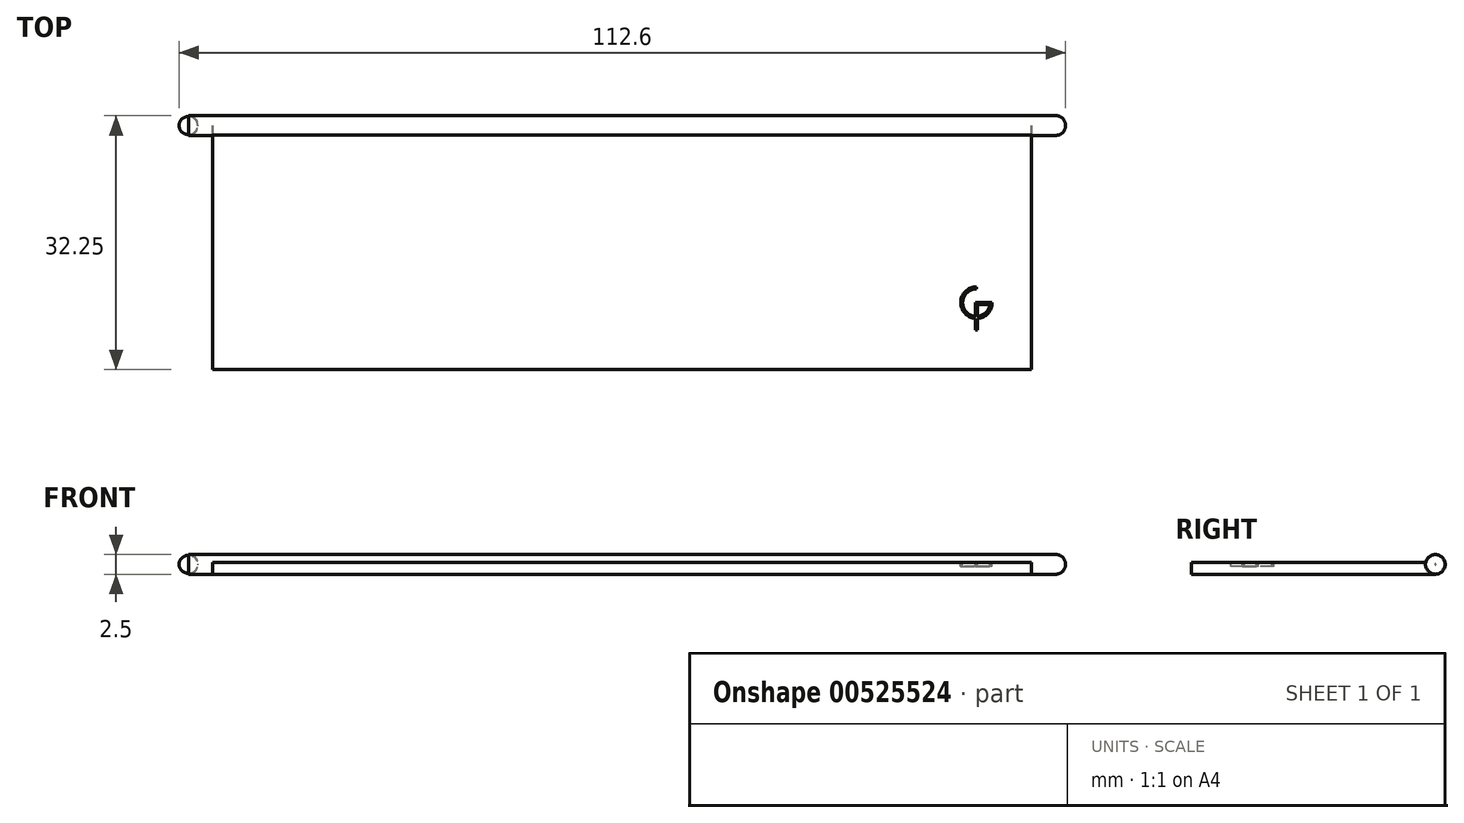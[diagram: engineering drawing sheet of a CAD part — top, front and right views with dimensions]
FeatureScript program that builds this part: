
annotation { "Feature Type Name" : "Feature", "Feature Type Description" : "" }
export const myFeature = defineFeature(function(context is Context, id is Id, definition is map)
    precondition{}
    {
        {
            var Q0;
            Q0=qCreatedBy(makeId("Right.planeOp"),FACE);
            var sketch = newSketch(context, id + "F0", { "sketchPlane" : qUnion([Q0])});
            skLineSegment(sketch, "E0.bottom", {"start": v(0, 0) * mm, "end": v(-31, 0) * mm});
            skLineSegment(sketch, "E0.top", {"start": v(0, 1.5) * mm, "end": v(-31, 1.5) * mm});
            skLineSegment(sketch, "E0.right", {"start": v(-31, 0) * mm, "end": v(-31, 1.5) * mm});
            skCircle(sketch, "E1", {"center": v(0, 1.25) * mm, "radius": 1.25 * mm});
            skPoint(sketch, "E1.second.point", {"position": v(0.68, 0.2) * mm});
            skPoint(sketch, "E1.third.point", {"position": v(-0.22, 2.48) * mm});
            skLineSegment(sketch, "E2", {"start": v(0, 1.5) * mm, "end": v(0, 0) * mm});
            skSolve(sketch);
        }
        {
            var Q0;
            {var subQ0=sQuery(id+"F0.wireOp",EDGE,"E0.bottom");Q0=makeQuery(id+"F0.imprint","IMPRINT",FACE,{"disambiguationData":[TD([[makeQuery(id+"F0.imprint","IMPRINT",EDGE,{"derivedFrom":subQ0}),-1.0]])]});}
            extrude(context, id + "F1", {"entities" : qUnion([Q0]), "oppositeDirection" : true, "depth" : 104 * mm, "offsetDistance" : 25 * mm});
        }
        {
            var Q0;
            {var subQ0=sQuery(id+"F0.wireOp",EDGE,"E2");Q0=makeQuery(id+"F0.imprint","IMPRINT",FACE,{"disambiguationData":[TD([[makeQuery(id+"F0.imprint","IMPRINT",EDGE,{"derivedFrom":subQ0}),-1.0]])]});}
            var Q1;
            {var subQ0=sQuery(id+"F0.wireOp",EDGE,"E2");Q1=makeQuery(id+"F0.imprint","IMPRINT",FACE,{"disambiguationData":[TD([[makeQuery(id+"F0.imprint","IMPRINT",EDGE,{"derivedFrom":subQ0}),1.0]])]});}
            extrude(context, id + "F2", {"entities" : qUnion([Q0, Q1]), "operationType" : NewBodyOperationType.ADD, "depth" : 4.3 * mm, "offsetDistance" : 25 * mm, "hasSecondDirection" : true, "secondDirectionOppositeDirection" : true, "secondDirectionDepth" : 108.3 * mm});
        }
        {
            var Q0;
            Q0=makeQuery(id+"F2.opExtrude","CAP_FACE",FACE,{"disambiguationData":[OSD([sQuery(id+"F0.wireOp",EDGE,"E1")])],"isStart":false});
            var Q1;
            Q1=makeQuery(id+"F2.opExtrude","CAP_FACE",FACE,{"disambiguationData":[OSD([sQuery(id+"F0.wireOp",EDGE,"E1")])],"isStart":true});
            fillet(context, id + "F3", {"entities" : qUnion([Q0, Q1]), "radius" : 1.2 * mm, "tangentPropagation" : true, "allowEdgeOverflow" : false});
        }
        {
            var Q0;
            Q0=makeQuery(id+"F1.opExtrude","SWEPT_FACE",FACE,{"disambiguationData":[OSD([sQuery(id+"F0.wireOp",EDGE,"E0.top")])]});
            var sketch = newSketch(context, id + "F4", { "sketchPlane" : qUnion([Q0])});
            skLineSegment(sketch, "E3.bottom", {"start": v(-7, -20.5) * mm, "end": v(-5, -20.5) * mm, "construction": true});
            skLineSegment(sketch, "E3.top", {"start": v(-7, -22.5) * mm, "end": v(-5, -22.5) * mm, "construction": true});
            skLineSegment(sketch, "E3.left", {"start": v(-7, -20.5) * mm, "end": v(-7, -22.5) * mm, "construction": true});
            skLineSegment(sketch, "E3.right", {"start": v(-5, -20.5) * mm, "end": v(-5, -22.5) * mm, "construction": true});
            skArc(sketch, "E4", {"start": v(-7, -20.5) * mm, "mid": v(-8.41, -23.91) * mm, "end": v(-5, -22.5) * mm});
            skLineSegment(sketch, "E5", {"start": v(-7, -20.5) * mm, "end": v(-7, -20.75) * mm});
            skLineSegment(sketch, "E6", {"start": v(-5, -22.5) * mm, "end": v(-5.25, -22.5) * mm});
            skArc(sketch, "E7", {"start": v(-7, -20.75) * mm, "mid": v(-8.24, -23.74) * mm, "end": v(-5.25, -22.5) * mm});
            skLineSegment(sketch, "E8", {"start": v(-5.25, -22.5) * mm, "end": v(-7.12, -22.5) * mm});
            skLineSegment(sketch, "E9", {"start": v(-7.12, -22.5) * mm, "end": v(-7.12, -26) * mm});
            skLineSegment(sketch, "E10", {"start": v(-7.12, -26) * mm, "end": v(-6.87, -26) * mm});
            skLineSegment(sketch, "E11", {"start": v(-5.27, -22.75) * mm, "end": v(-6.87, -22.75) * mm});
            skLineSegment(sketch, "E12", {"start": v(-6.87, -22.75) * mm, "end": v(-6.87, -26) * mm});
            skSolve(sketch);
        }
        {
            var Q0;
            Q0 = qSketchRegion(id + "F4", true);
            extrude(context, id + "F5", {"entities" : qUnion([Q0]), "operationType" : NewBodyOperationType.REMOVE, "oppositeDirection" : true, "depth" : .5 * mm, "offsetDistance" : 25 * mm});
        }
    });
